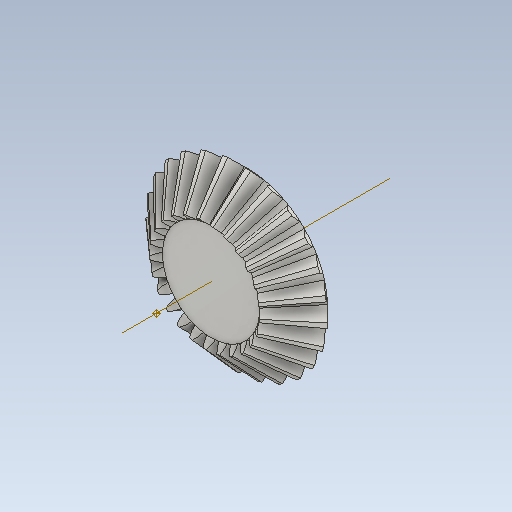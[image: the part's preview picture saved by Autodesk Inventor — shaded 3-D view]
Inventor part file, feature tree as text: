
AUTODESK INVENTOR PART (.ipt)
format: ipt  version: 2023 (Build 270158000, 158)  size: 566,272 bytes
history: native  units: mm
features: other x24, loft x2, pattern_circular x2, sketch x1
ambient origin geometry x6: Origin, XZ Plane, X Axis, Y Axis, Z Axis, Center Point
bodies: Solid1 (feature_tree)
feature tree (29):
  other  "Top Point"
  other  "Mesh Plane2"
  other  "Teeth Body"
  other  "Start Point"
  other  "Tooth Plane"
  other  "Start Sketch"
  other  "End Point"
  other  "3D Sketch Right"
  other  "End Plane Right"
  loft  "Loft Right"
  pattern_circular  "Circular Pattern Right"  [2 undecoded]
  other  "3D Sketch Left"
  other  "End Plane Left"
  loft  "Loft Left"
  pattern_circular  "Circular Pattern Left"  [2 undecoded]
  other  "Fix Body"
  other  "Mesh Plane"
  other  "Top Plane"
  other  "Teeth Body Sketch"
  other  "End Plane"
  other  "End Sketch"
  other  "Helical Curve Left"
  other  "End Sketch Left"
  other  "Body Sketch"
  sketch  "Sketch6"  dims[d0=25.4mm d1=23.675791mm d2=26.836841mm d3=7.1mm d4=11.98158mm d5=90.0deg d7=6.490689mm d8=6.790786mm d9=15.450402mm d11=7.21176mm d12=3.884455mm d15=4.064053mm d16=9.246537mm d17=0.0mm d18=90.0deg d19=0.0mm d20=90.0deg d21=250.0mm d22=360.0deg d26=124.383686mm d27=5.099484mm d28=25.4mm d29=-7.853982mm d30=3.884455mm d31=4.064053mm d32=9.246537mm d35=0.0mm d37=0.0mm d39=0.0mm d40=90.0deg d41=250.0mm d42=360.0deg d46=90.0deg d47=90.0deg d48=0.0mm d49=0.0mm d50=90.0deg d51=1.256637mm d52=0.0mm d53=0.0mm d54=0.0mm d56=5.737655mm d57=19.647072mm d58=16.473088mm d59=11.758101mm d60=9.85858mm d61=11.758101mm d62=9.85858mm d63=90.0deg d64=90.0deg d65=124.383686mm d66=31.5mm d67=25.4mm d68=-7.853982mm d69=5.099484mm d70=4.064053mm d71=9.246537mm d72=3.884455mm d73=9.85858mm d74=11.758101mm d75=0.0mm d76=90.0deg d77=0.0mm d78=90.0deg d79=0.0mm d80=90.0deg d81=250.0mm d82=360.0deg d84=10.0mm d85=20.0mm d86=20.0mm d87=10.0mm d88=0.0mm d89=0.0mm]
  other  "Srf1"
  other  "Helical Curve Right"
  other  "End Sketch Right"
  other  "Pitch Diameter"
note: 4 required parameter values undecoded (feature->parameter linkage not recoverable at this tier; creation-order binding heuristic only, values carry confidence <= 0.55)
